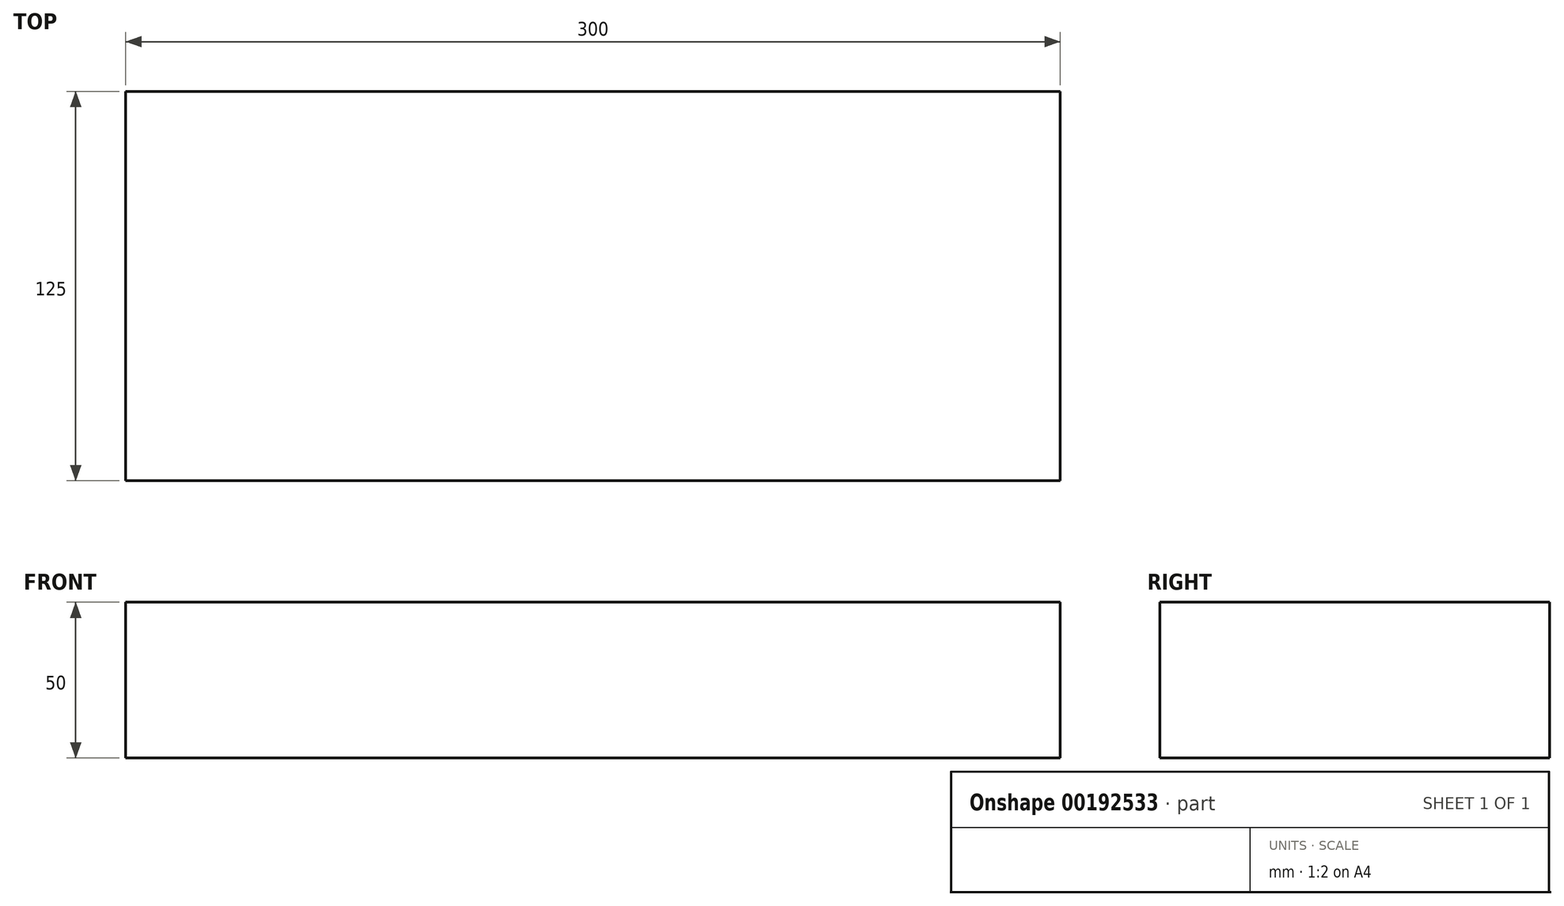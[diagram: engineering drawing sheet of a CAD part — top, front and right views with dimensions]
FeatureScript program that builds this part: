
annotation { "Feature Type Name" : "Feature", "Feature Type Description" : "" }
export const myFeature = defineFeature(function(context is Context, id is Id, definition is map)
    precondition{}
    {
        {
            var Q0;
            Q0=qCreatedBy(makeId("Top.planeOp"),FACE);
            var sketch = newSketch(context, id + "F0", { "sketchPlane" : qUnion([Q0])});
            skLineSegment(sketch, "E0.bottom", {"start": v(150, 62.5) * mm, "end": v(-150, 62.5) * mm});
            skLineSegment(sketch, "E0.top", {"start": v(150, -62.5) * mm, "end": v(-150, -62.5) * mm});
            skLineSegment(sketch, "E0.left", {"start": v(150, 62.5) * mm, "end": v(150, -62.5) * mm});
            skLineSegment(sketch, "E0.right", {"start": v(-150, 62.5) * mm, "end": v(-150, -62.5) * mm});
            skPoint(sketch, "E0.middle", {"position": v(0, 0) * mm});
            skSolve(sketch);
        }
        {
            var Q0;
            Q0 = qSketchRegion(id + "F0", true);
            extrude(context, id + "F1", {"entities" : qUnion([Q0]), "depth" : 50 * mm});
        }
    });
